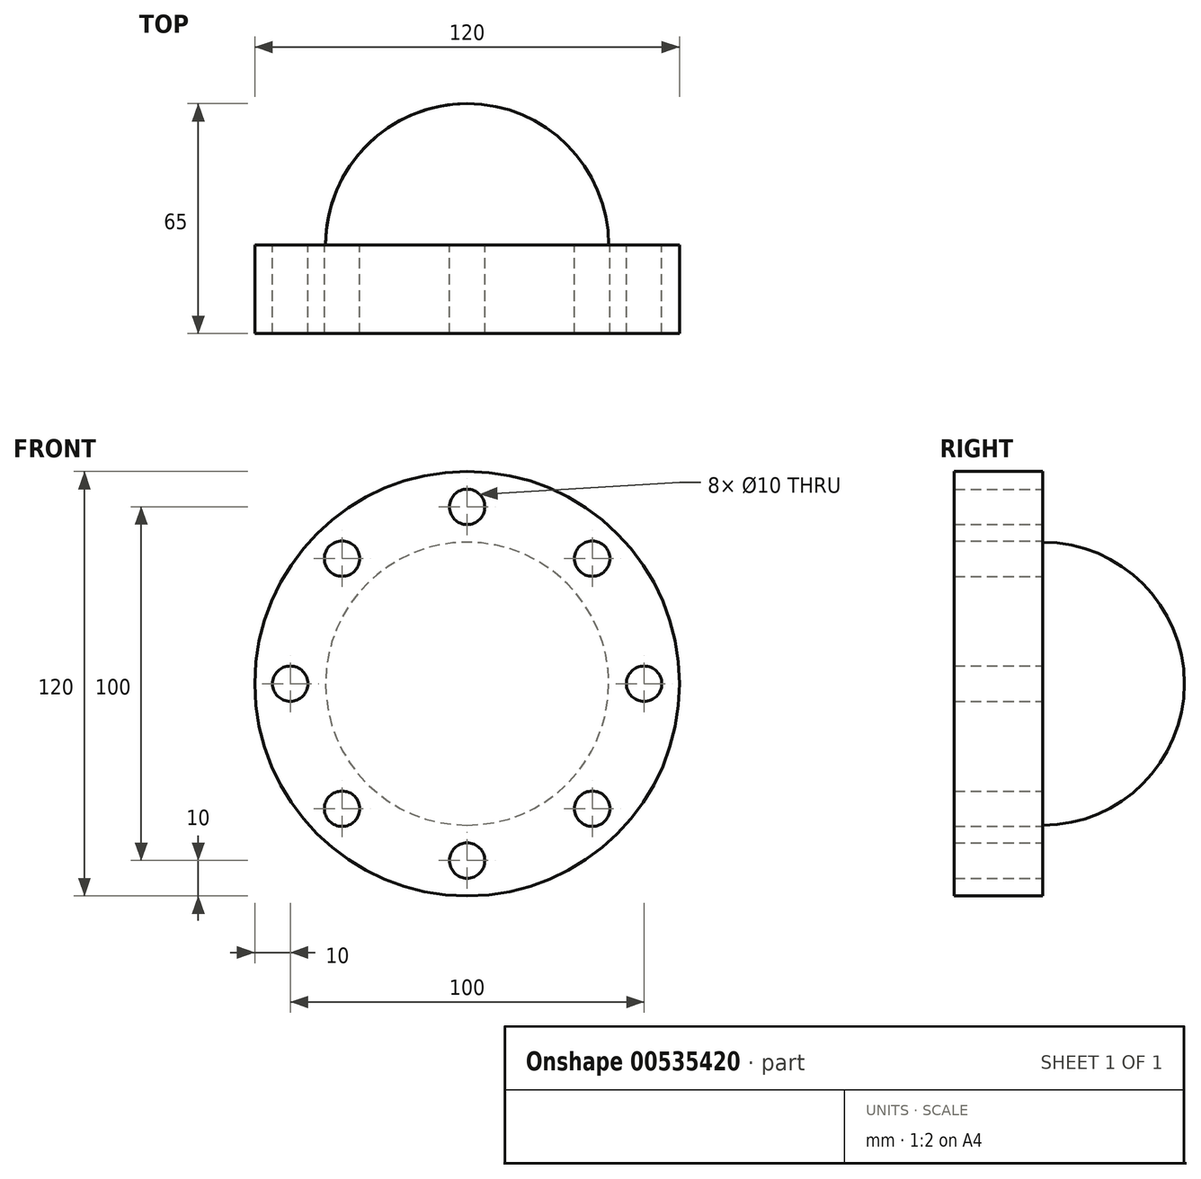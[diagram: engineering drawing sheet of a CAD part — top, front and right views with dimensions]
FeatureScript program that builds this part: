
annotation { "Feature Type Name" : "Feature", "Feature Type Description" : "" }
export const myFeature = defineFeature(function(context is Context, id is Id, definition is map)
    precondition{}
    {
        {
            var Q0;
            Q0=qCreatedBy(makeId("Front.planeOp"),FACE);
            var sketch = newSketch(context, id + "F0", { "sketchPlane" : qUnion([Q0])});
            skCircle(sketch, "E0", {"center": v(0, 0) * mm, "radius": 60 * mm});
            skCircle(sketch, "E1", {"center": v(0, 50) * mm, "radius": 5 * mm});
            skCircle(sketch, "E2.1.0", {"center": v(-35.36, 35.36) * mm, "radius": 5 * mm});
            skCircle(sketch, "E2.2.0", {"center": v(-50, 0) * mm, "radius": 5 * mm});
            skCircle(sketch, "E2.3.0", {"center": v(-35.36, -35.36) * mm, "radius": 5 * mm});
            skCircle(sketch, "E2.4.0", {"center": v(0, -50) * mm, "radius": 5 * mm});
            skCircle(sketch, "E2.5.0", {"center": v(35.36, -35.36) * mm, "radius": 5 * mm});
            skCircle(sketch, "E2.6.0", {"center": v(50, 0) * mm, "radius": 5 * mm});
            skCircle(sketch, "E2.7.0", {"center": v(35.36, 35.36) * mm, "radius": 5 * mm});
            skSolve(sketch);
        }
        {
            var Q0;
            Q0 = qSketchRegion(id + "F0", true);
            extrude(context, id + "F1", {"entities" : qUnion([Q0]), "depth" : 25 * mm, "offsetDistance" : 25 * mm});
        }
        {
            var Q0;
            Q0=qCreatedBy(makeId("Top.planeOp"),FACE);
            var sketch = newSketch(context, id + "F2", { "sketchPlane" : qUnion([Q0])});
            skLineSegment(sketch, "E3", {"start": v(60, 0) * mm, "end": v(60, -25) * mm});
            skLineSegment(sketch, "E4", {"start": v(-60, -25) * mm, "end": v(-60, 0) * mm});
            skArc(sketch, "E5", {"start": v(0, 40) * mm, "mid": v(-28.28, 28.28) * mm, "end": v(-40, 0) * mm});
            skLineSegment(sketch, "E6", {"start": v(0, 0) * mm, "end": v(0, 40) * mm});
            skLineSegment(sketch, "E7", {"start": v(0, 0) * mm, "end": v(-40, 0) * mm});
            skSolve(sketch);
        }
        {
            var Q0;
            Q0=makeQuery(id+"F2.imprint","IMPRINT",FACE,{"disambiguationData":[TD([[makeQuery(id+"F2.imprint","IMPRINT",EDGE,{"derivedFrom":sQuery(id+"F2.wireOp",EDGE,"E5")}),1.0]])]});
            var Q1;
            Q1=makeQuery(id+"F1.opExtrude","SWEPT_FACE",FACE,{"disambiguationData":[OSD([sQuery(id+"F0.wireOp",EDGE,"E0")])]});
            revolve(context, id + "F3", {"operationType" : NewBodyOperationType.ADD, "entities" : qUnion([Q0]), "axis" : qUnion([Q1]), "revolveType" : RevolveType.FULL});
        }
    });
